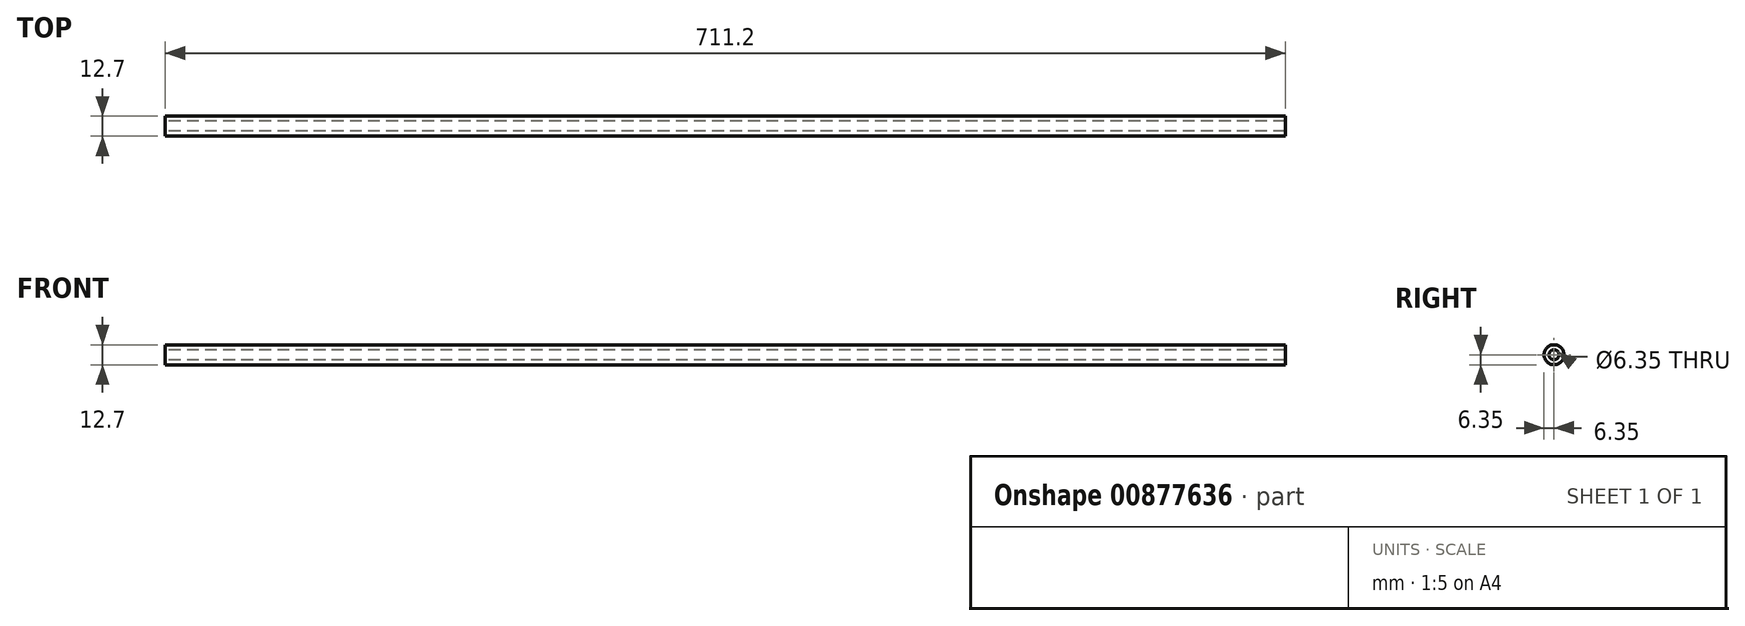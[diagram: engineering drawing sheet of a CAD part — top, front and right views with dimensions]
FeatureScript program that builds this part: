
annotation { "Feature Type Name" : "Feature", "Feature Type Description" : "" }
export const myFeature = defineFeature(function(context is Context, id is Id, definition is map)
    precondition{}
    {
        {
            var Q0;
            Q0=qCreatedBy(makeId("Right.planeOp"),FACE);
            var sketch = newSketch(context, id + "F0", { "sketchPlane" : qUnion([Q0])});
            skCircle(sketch, "E0", {"center": v(0, 0) * mm, "radius": 6.35 * mm});
            skCircle(sketch, "E1", {"center": v(0, 0) * mm, "radius": 3.18 * mm});
            skSolve(sketch);
        }
        {
            var Q0;
            Q0=qSketchRegion(id+"F0",true);
            extrude(context, id + "F1", {"entities" : qUnion([Q0]), "depth" : 711.2 * mm, "offsetDistance" : 25.4 * mm});
        }
    });
